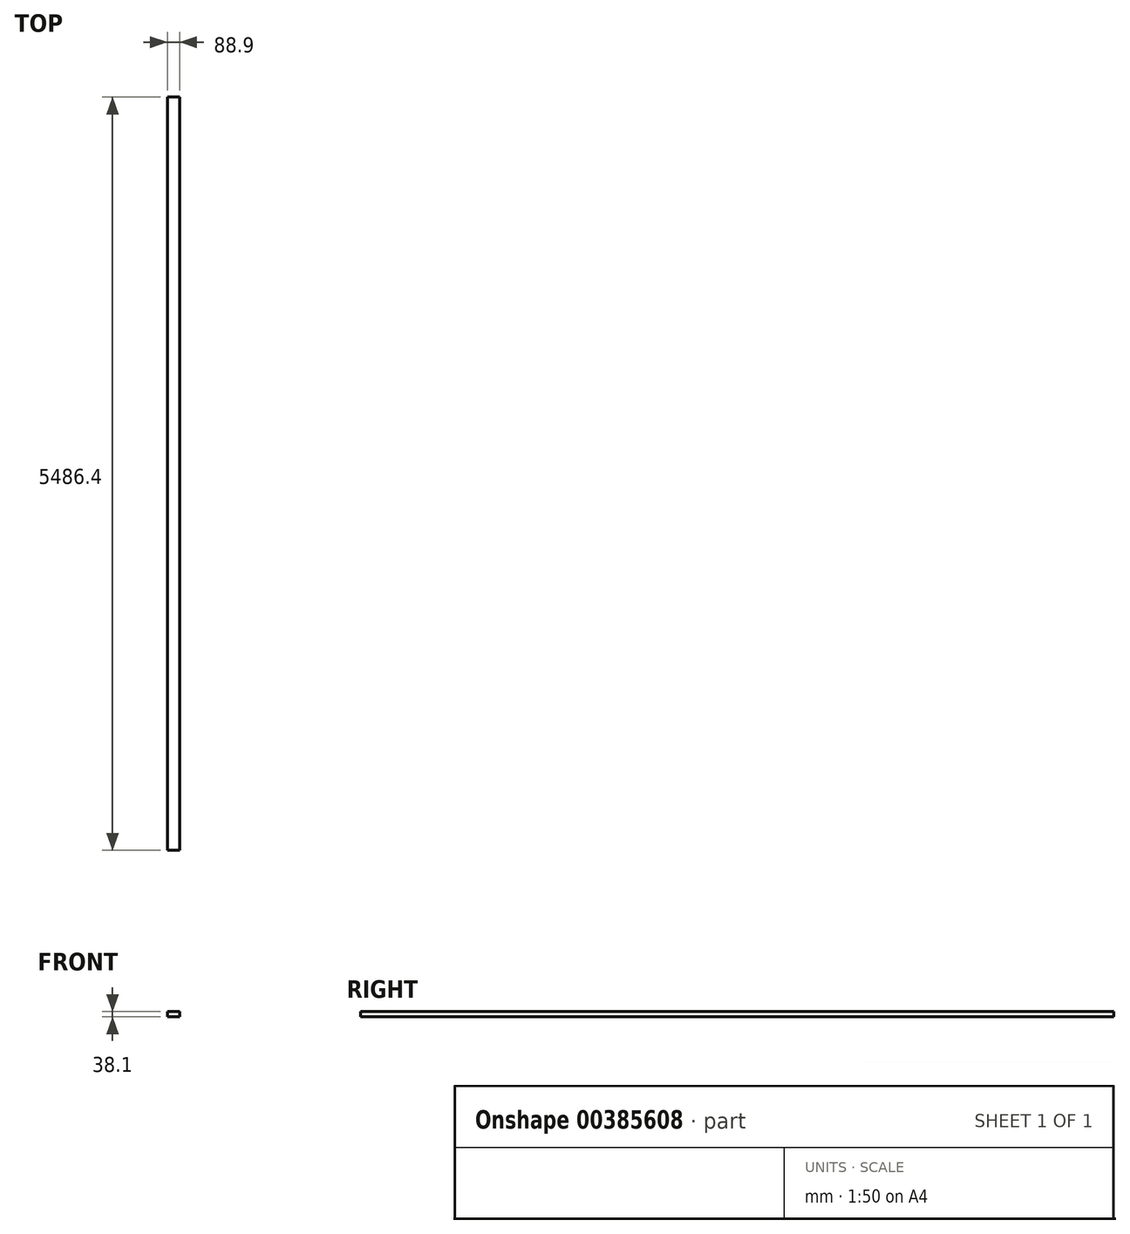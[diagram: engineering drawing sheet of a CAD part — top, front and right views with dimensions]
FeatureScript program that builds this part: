
annotation { "Feature Type Name" : "Feature", "Feature Type Description" : "" }
export const myFeature = defineFeature(function(context is Context, id is Id, definition is map)
    precondition{}
    {
        {
            var Q0;
            Q0=qCreatedBy(makeId("Front.planeOp"),FACE);
            var sketch = newSketch(context, id + "F0", { "sketchPlane" : qUnion([Q0])});
            skLineSegment(sketch, "E0.bottom", {"start": v(0, 2.03) * mm, "end": v(88.9, 2.03) * mm});
            skLineSegment(sketch, "E0.top", {"start": v(0, 40.13) * mm, "end": v(88.9, 40.13) * mm});
            skLineSegment(sketch, "E0.left", {"start": v(0, 2.03) * mm, "end": v(0, 40.13) * mm});
            skLineSegment(sketch, "E0.right", {"start": v(88.9, 2.03) * mm, "end": v(88.9, 40.13) * mm});
            skSolve(sketch);
        }
        {
            var Q0;
            Q0 = qSketchRegion(id + "F0", true);
            extrude(context, id + "F1", {"entities" : qUnion([Q0]), "depth" : 5486.4 * mm});
        }
    });
